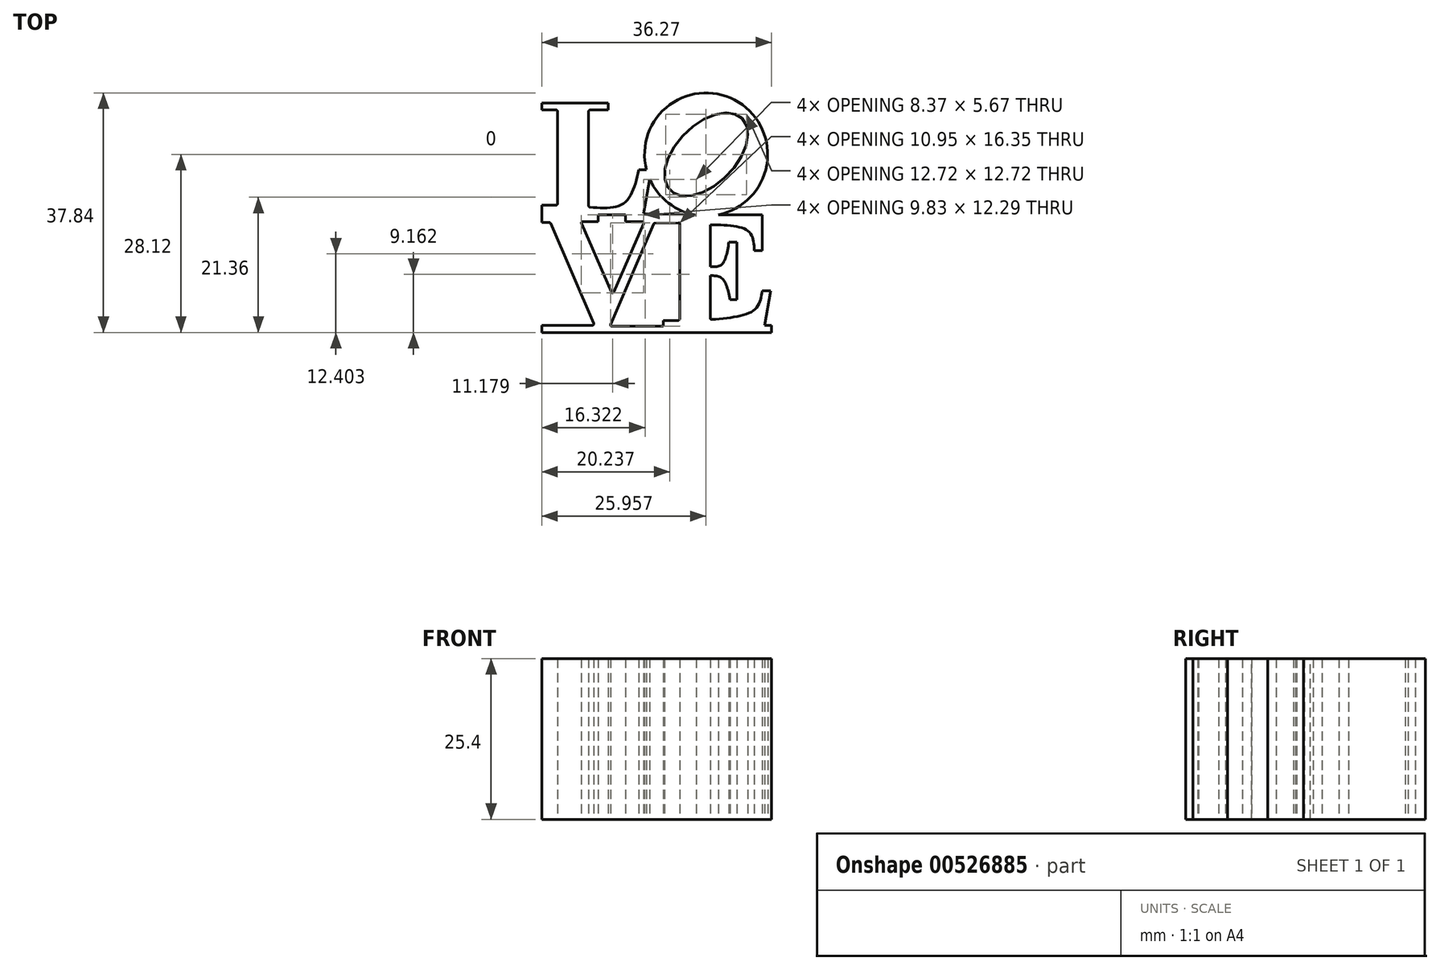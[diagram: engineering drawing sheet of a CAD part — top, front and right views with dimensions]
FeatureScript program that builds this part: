
annotation { "Feature Type Name" : "Feature", "Feature Type Description" : "" }
export const myFeature = defineFeature(function(context is Context, id is Id, definition is map)
    precondition{}
    {
        {
            var Q0;
            Q0=qCreatedBy(makeId("Top.planeOp"),FACE);
            var sketch = newSketch(context, id + "F0", { "sketchPlane" : qUnion([Q0])});
            skArc(sketch, "E0", {"start": v(-13.82, 22.1) * mm, "mid": v(-10.65, 39.87) * mm, "end": v(-25.2, 29.2) * mm});
            skEllipse(sketch, "E1", {"center": v(-15.8, 31.62) * mm, "majorRadius": 8.03 * mm, "minorRadius": 4.69 * mm, "majorAxis": v(0.7, 0.7)});
            skLineSegment(sketch, "E2", {"start": v(-41.75, 39.76) * mm, "end": v(-31.28, 39.76) * mm});
            skLineSegment(sketch, "E3", {"start": v(-31.28, 39.76) * mm, "end": v(-31.28, 38.63) * mm});
            skLineSegment(sketch, "E4", {"start": v(-31.28, 38.63) * mm, "end": v(-34.14, 38.63) * mm});
            skLineSegment(sketch, "E5", {"start": v(-41.75, 38.63) * mm, "end": v(-41.75, 39.76) * mm});
            skLineSegment(sketch, "E6", {"start": v(-39.26, 38.43) * mm, "end": v(-39.26, 23.81) * mm});
            skLineSegment(sketch, "E7", {"start": v(-39.46, 23.61) * mm, "end": v(-41.75, 23.61) * mm});
            skLineSegment(sketch, "E8", {"start": v(-41.75, 23.61) * mm, "end": v(-41.75, 20.85) * mm});
            skLineSegment(sketch, "E9", {"start": v(-41.75, 20.85) * mm, "end": v(-40.55, 20.85) * mm});
            skLineSegment(sketch, "E10", {"start": v(-40.36, 20.73) * mm, "end": v(-33.54, 4.9) * mm});
            skLineSegment(sketch, "E11", {"start": v(-33.72, 4.63) * mm, "end": v(-41.75, 4.63) * mm});
            skLineSegment(sketch, "E12", {"start": v(-41.75, 4.63) * mm, "end": v(-41.75, 3.5) * mm});
            skLineSegment(sketch, "E13", {"start": v(-41.75, 3.5) * mm, "end": v(-5.48, 3.5) * mm});
            skLineSegment(sketch, "E14", {"start": v(-5.48, 3.5) * mm, "end": v(-5.48, 4.63) * mm});
            skLineSegment(sketch, "E15", {"start": v(-5.48, 4.63) * mm, "end": v(-6.54, 4.63) * mm});
            skLineSegment(sketch, "E16", {"start": v(-6.54, 4.63) * mm, "end": v(-5.62, 10.08) * mm});
            skLineSegment(sketch, "E17", {"start": v(-5.62, 10.08) * mm, "end": v(-6.93, 10.08) * mm});
            skLineSegment(sketch, "E18", {"start": v(-24.06, 20.63) * mm, "end": v(-30.89, 4.76) * mm});
            skLineSegment(sketch, "E19", {"start": v(-30.7, 4.48) * mm, "end": v(-22.56, 4.48) * mm});
            skLineSegment(sketch, "E20", {"start": v(-22.56, 4.48) * mm, "end": v(-22.56, 5.4) * mm});
            skLineSegment(sketch, "E21", {"start": v(-22.56, 5.4) * mm, "end": v(-20.26, 5.4) * mm});
            skLineSegment(sketch, "E22", {"start": v(-19.96, 5.7) * mm, "end": v(-19.96, 20.64) * mm});
            skLineSegment(sketch, "E23", {"start": v(-20.16, 20.84) * mm, "end": v(-23.88, 20.75) * mm});
            skLineSegment(sketch, "E24", {"start": v(-35.29, 20.99) * mm, "end": v(-32.84, 20.99) * mm});
            skLineSegment(sketch, "E25", {"start": v(-25.67, 20.7) * mm, "end": v(-30.39, 9.88) * mm});
            skLineSegment(sketch, "E26", {"start": v(-30.75, 9.88) * mm, "end": v(-35.47, 20.7) * mm});
            skLineSegment(sketch, "E27", {"start": v(-32.84, 20.99) * mm, "end": v(-32.84, 22.05) * mm});
            skLineSegment(sketch, "E28", {"start": v(-32.84, 22.05) * mm, "end": v(-28.5, 22.05) * mm});
            skLineSegment(sketch, "E29", {"start": v(-28.5, 22.05) * mm, "end": v(-28.5, 20.99) * mm});
            skLineSegment(sketch, "E30", {"start": v(-24.68, 27.7) * mm, "end": v(-25.7, 22.24) * mm});
            skLineSegment(sketch, "E31", {"start": v(-25.7, 22.24) * mm, "end": v(-17.33, 22.02) * mm});
            skLineSegment(sketch, "E32", {"start": v(-25.2, 29.2) * mm, "end": v(-26.42, 29.2) * mm});
            skLineSegment(sketch, "E33", {"start": v(-34.34, 23.49) * mm, "end": v(-34.34, 38.43) * mm});
            skFitSpline(sketch, "E34", {"points": [v(-34.34, 23.3) * mm, v(-28.74, 23.93) * mm, v(-26.42, 29.2) * mm], "startDerivative": vector(12.9, -1.03) * mm, "endDerivative": vector(2.94, 12.78) * mm});
            skLineSegment(sketch, "E35", {"start": v(-13.82, 22.1) * mm, "end": v(-6.92, 22.1) * mm});
            skLineSegment(sketch, "E36", {"start": v(-6.92, 22.1) * mm, "end": v(-6.92, 16.45) * mm});
            skLineSegment(sketch, "E37", {"start": v(-6.92, 16.45) * mm, "end": v(-8.18, 16.45) * mm});
            skLineSegment(sketch, "E38", {"start": v(-12.18, 17.75) * mm, "end": v(-10.93, 17.75) * mm});
            skLineSegment(sketch, "E39", {"start": v(-10.93, 17.75) * mm, "end": v(-10.93, 8.68) * mm});
            skLineSegment(sketch, "E40", {"start": v(-10.93, 8.68) * mm, "end": v(-11.99, 8.68) * mm});
            skLineSegment(sketch, "E41", {"start": v(-15.13, 20.5) * mm, "end": v(-15.13, 13.91) * mm});
            skFitSpline(sketch, "E42", {"points": [v(-15.13, 13.91) * mm, v(-13.33, 14.23) * mm, v(-12.18, 17.75) * mm], "startDerivative": vector(4.86, -0.32) * mm, "endDerivative": vector(1.25, 7.54) * mm});
            skFitSpline(sketch, "E43", {"points": [v(-8.18, 16.45) * mm, v(-9.1, 19.46) * mm, v(-15.13, 20.5) * mm], "startDerivative": vector(-0.53, 8.34) * mm, "endDerivative": vector(-12.7, 0.22) * mm});
            skFitSpline(sketch, "E44", {"points": [v(-15.13, 12.47) * mm, v(-13.28, 12.06) * mm, v(-11.99, 8.68) * mm], "startDerivative": vector(4.86, 0.04) * mm, "endDerivative": vector(1.6, -7.22) * mm});
            skFitSpline(sketch, "E45", {"points": [v(-6.93, 10.08) * mm, v(-8.18, 7.08) * mm, v(-15.13, 5.53) * mm], "startDerivative": vector(-1.38, -8.41) * mm, "endDerivative": vector(-14.2, -1.16) * mm});
            skLineSegment(sketch, "E46.trimOffspring", {"start": v(-15.13, 12.47) * mm, "end": v(-15.13, 5.75) * mm});
            skArc(sketch, "E47.trimOffspring", {"start": v(-24.68, 27.7) * mm, "mid": v(-21.73, 23.92) * mm, "end": v(-17.33, 22.02) * mm});
            skLineSegment(sketch, "E48.trimOffspring", {"start": v(-28.5, 20.99) * mm, "end": v(-25.86, 20.99) * mm});
            skLineSegment(sketch, "E49.trimOffspring", {"start": v(-39.46, 38.63) * mm, "end": v(-41.75, 38.63) * mm});
            skPoint(sketch, "E50.visualSharp", {"position": v(-34.34, 38.63) * mm});
            skArc(sketch, "E50.filletArc", {"start": v(-34.14, 38.63) * mm, "mid": v(-34.28, 38.57) * mm, "end": v(-34.34, 38.43) * mm});
            skPoint(sketch, "E51.visualSharp", {"position": v(-39.26, 38.63) * mm});
            skArc(sketch, "E51.filletArc", {"start": v(-39.26, 38.43) * mm, "mid": v(-39.32, 38.57) * mm, "end": v(-39.46, 38.63) * mm});
            skPoint(sketch, "E52.visualSharp", {"position": v(-39.26, 23.61) * mm});
            skArc(sketch, "E52.filletArc", {"start": v(-39.46, 23.61) * mm, "mid": v(-39.32, 23.67) * mm, "end": v(-39.26, 23.81) * mm});
            skArc(sketch, "E53.filletArc", {"start": v(-34.34, 23.49) * mm, "mid": v(-34.28, 23.35) * mm, "end": v(-34.15, 23.29) * mm});
            skPoint(sketch, "E54.visualSharp", {"position": v(-35.59, 20.99) * mm});
            skArc(sketch, "E54.filletArc", {"start": v(-35.29, 20.99) * mm, "mid": v(-35.45, 20.9) * mm, "end": v(-35.47, 20.7) * mm});
            skPoint(sketch, "E55.visualSharp", {"position": v(-40.41, 20.85) * mm});
            skArc(sketch, "E55.filletArc", {"start": v(-40.36, 20.73) * mm, "mid": v(-40.44, 20.82) * mm, "end": v(-40.55, 20.85) * mm});
            skPoint(sketch, "E56.visualSharp", {"position": v(-25.55, 20.99) * mm});
            skArc(sketch, "E56.filletArc", {"start": v(-25.67, 20.7) * mm, "mid": v(-25.7, 20.9) * mm, "end": v(-25.86, 20.99) * mm});
            skPoint(sketch, "E57.visualSharp", {"position": v(-30.57, 9.46) * mm});
            skArc(sketch, "E57.filletArc", {"start": v(-30.75, 9.88) * mm, "mid": v(-30.57, 9.76) * mm, "end": v(-30.39, 9.88) * mm});
            skPoint(sketch, "E58.visualSharp", {"position": v(-31, 4.48) * mm});
            skArc(sketch, "E58.filletArc", {"start": v(-30.89, 4.76) * mm, "mid": v(-30.87, 4.57) * mm, "end": v(-30.7, 4.48) * mm});
            skPoint(sketch, "E59.visualSharp", {"position": v(-33.42, 4.63) * mm});
            skArc(sketch, "E59.filletArc", {"start": v(-33.72, 4.63) * mm, "mid": v(-33.56, 4.72) * mm, "end": v(-33.54, 4.9) * mm});
            skPoint(sketch, "E60.visualSharp", {"position": v(-24, 20.75) * mm});
            skArc(sketch, "E60.filletArc", {"start": v(-23.88, 20.75) * mm, "mid": v(-23.99, 20.72) * mm, "end": v(-24.06, 20.63) * mm});
            skPoint(sketch, "E61.visualSharp", {"position": v(-19.96, 20.84) * mm});
            skArc(sketch, "E61.filletArc", {"start": v(-19.96, 20.64) * mm, "mid": v(-20.02, 20.78) * mm, "end": v(-20.16, 20.84) * mm});
            skArc(sketch, "E62.filletArc", {"start": v(-15.13, 5.75) * mm, "mid": v(-15.07, 5.6) * mm, "end": v(-14.91, 5.55) * mm});
            skPoint(sketch, "E63.visualSharp", {"position": v(-19.96, 5.4) * mm});
            skArc(sketch, "E63.filletArc", {"start": v(-20.26, 5.4) * mm, "mid": v(-20.04, 5.48) * mm, "end": v(-19.96, 5.7) * mm});
            skSolve(sketch);
        }
        {
            var Q0;
            Q0=makeQuery(id+"F0.imprint","IMPRINT",FACE,{"disambiguationData":[TD([[makeQuery(id+"F0.imprint","IMPRINT",EDGE,{"derivedFrom":sQuery(id+"F0.wireOp",EDGE,"E0")}),1.0]])]});
            extrude(context, id + "F1", {"entities" : qUnion([Q0]), "depth" : 25.4 * mm, "offsetDistance" : 25.4 * mm});
        }
    });
